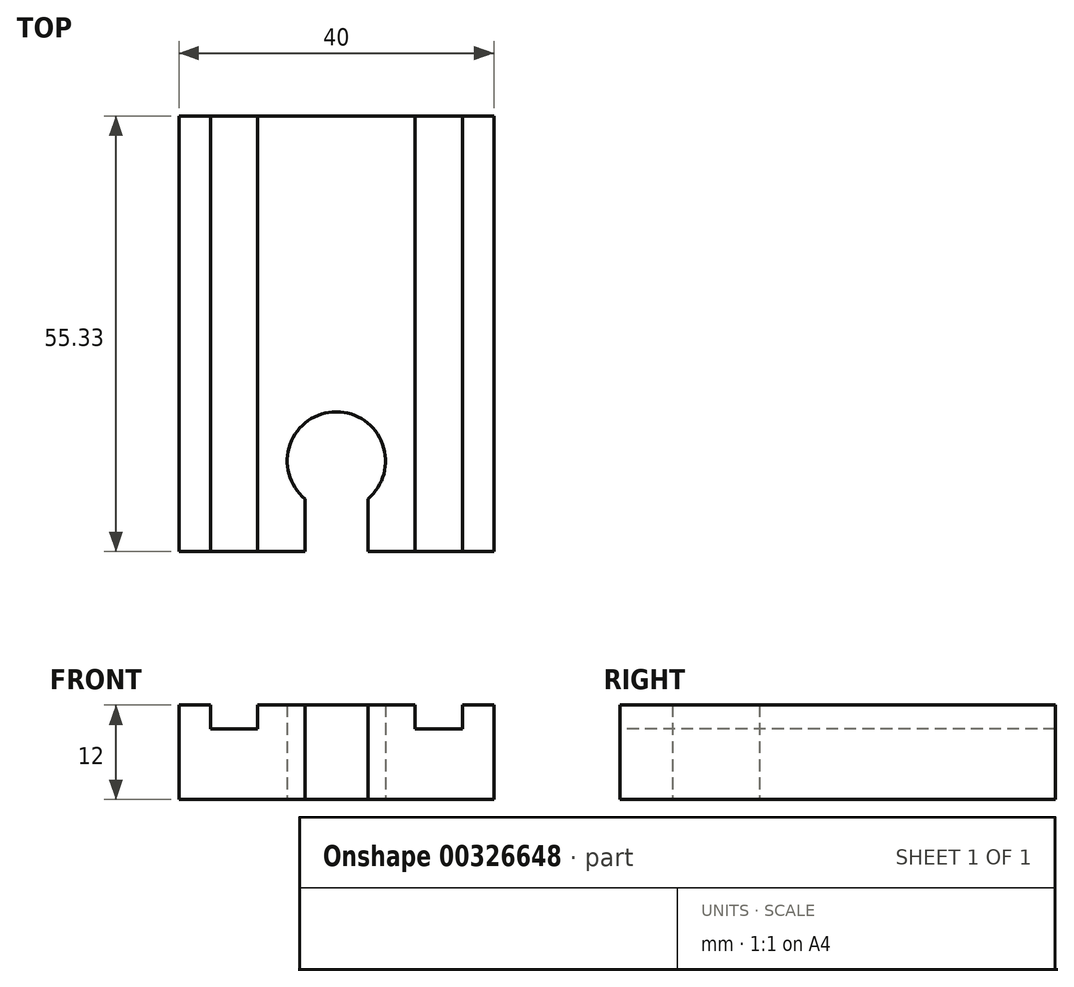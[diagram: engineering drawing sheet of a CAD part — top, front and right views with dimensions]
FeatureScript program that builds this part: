
annotation { "Feature Type Name" : "Feature", "Feature Type Description" : "" }
export const myFeature = defineFeature(function(context is Context, id is Id, definition is map)
    precondition{}
    {
        {
            var Q0;
            Q0=qCreatedBy(makeId("Top.planeOp"),FACE);
            var sketch = newSketch(context, id + "F0", { "sketchPlane" : qUnion([Q0])});
            skLineSegment(sketch, "E0.bottom", {"start": v(0, 0) * mm, "end": v(40, 0) * mm});
            skLineSegment(sketch, "E0.top", {"start": v(0, 55.33) * mm, "end": v(40, 55.33) * mm});
            skLineSegment(sketch, "E0.left", {"start": v(0, 0) * mm, "end": v(0, 55.33) * mm});
            skLineSegment(sketch, "E0.right", {"start": v(40, 0) * mm, "end": v(40, 55.33) * mm});
            skLineSegment(sketch, "E1", {"start": v(4, 0) * mm, "end": v(4, 55.33) * mm, "construction": true});
            skLineSegment(sketch, "E2", {"start": v(10, 55.33) * mm, "end": v(10, 0) * mm, "construction": true});
            skLineSegment(sketch, "E3", {"start": v(30, 55.33) * mm, "end": v(30, 0) * mm, "construction": true});
            skLineSegment(sketch, "E4", {"start": v(36, 55.33) * mm, "end": v(36, 0) * mm, "construction": true});
            skPoint(sketch, "E5", {"position": v(20, 0) * mm});
            skPoint(sketch, "E6", {"position": v(20, 55.33) * mm});
            skLineSegment(sketch, "E7.right", {"start": v(17.5, 55.33) * mm, "end": v(17.5, 62.15) * mm});
            skLineSegment(sketch, "E8", {"start": v(22.5, 62.15) * mm, "end": v(22.5, 55.33) * mm});
            skLineSegment(sketch, "E9", {"start": v(20, 67.33) * mm, "end": v(20, 55.33) * mm, "construction": true});
            skLineSegment(sketch, "E10", {"start": v(20, 0) * mm, "end": v(20, 11.5) * mm, "construction": true});
            skLineSegment(sketch, "E11", {"start": v(16, 0) * mm, "end": v(16, 6.7) * mm});
            skLineSegment(sketch, "E12", {"start": v(24, 0) * mm, "end": v(24, 6.7) * mm});
            skArc(sketch, "E13", {"start": v(16, 6.7) * mm, "mid": v(20, 5.25) * mm, "end": v(24, 6.7) * mm, "construction": true});
            skArc(sketch, "E14", {"start": v(24, 6.7) * mm, "mid": v(20, 17.75) * mm, "end": v(16, 6.7) * mm});
            skArc(sketch, "E15", {"start": v(17.5, 62.15) * mm, "mid": v(20, 61.58) * mm, "end": v(22.5, 62.15) * mm, "construction": true});
            skArc(sketch, "E16", {"start": v(22.5, 62.15) * mm, "mid": v(20, 73.08) * mm, "end": v(17.5, 62.15) * mm});
            skSolve(sketch);
        }
        {
            var Q0;
            Q0=makeQuery(id+"F0.imprint","IMPRINT",FACE,{"disambiguationData":[TD([[makeQuery(id+"F0.imprint","IMPRINT",EDGE,{"derivedFrom":sQuery(id+"F0.wireOp",EDGE,"E0.bottom")}),1.0]])]});
            extrude(context, id + "F1", {"entities" : qUnion([Q0]), "depth" : 12 * mm});
        }
        {
            var Q0;
            Q0=makeQuery(id+"F1.opExtrude","CAP_FACE",FACE,{"disambiguationData":[OSD([sQuery(id+"F0.wireOp",EDGE,"E0.bottom"),sQuery(id+"F0.wireOp",EDGE,"E0.top"),sQuery(id+"F0.wireOp",EDGE,"E0.left"),sQuery(id+"F0.wireOp",EDGE,"E0.right")])],"isStart":false});
            var sketch = newSketch(context, id + "F2", { "sketchPlane" : qUnion([Q0])});
            skLineSegment(sketch, "E17.0", {"start": v(4, 0) * mm, "end": v(4, 55.33) * mm});
            skLineSegment(sketch, "E17.1", {"start": v(10, 55.33) * mm, "end": v(10, 0) * mm});
            skLineSegment(sketch, "E17.2", {"start": v(30, 55.33) * mm, "end": v(30, 0) * mm});
            skLineSegment(sketch, "E17.3", {"start": v(36, 55.33) * mm, "end": v(36, 0) * mm});
            skLineSegment(sketch, "E18", {"start": v(4, 55.33) * mm, "end": v(10, 55.33) * mm});
            skLineSegment(sketch, "E19", {"start": v(4, 0) * mm, "end": v(10, 0) * mm});
            skLineSegment(sketch, "E20", {"start": v(30, 0) * mm, "end": v(36, 0) * mm});
            skLineSegment(sketch, "E21", {"start": v(30, 55.33) * mm, "end": v(36, 55.33) * mm});
            skSolve(sketch);
        }
        {
            var Q0;
            Q0=makeQuery(id+"F2.imprint","IMPRINT",FACE,{"disambiguationData":[TD([[makeQuery(id+"F2.imprint","IMPRINT",EDGE,{"derivedFrom":sQuery(id+"F2.wireOp",EDGE,"E17.0")}),-1.0]])]});
            var Q1;
            Q1=makeQuery(id+"F2.imprint","IMPRINT",FACE,{"disambiguationData":[TD([[makeQuery(id+"F2.imprint","IMPRINT",EDGE,{"derivedFrom":sQuery(id+"F2.wireOp",EDGE,"E17.2")}),1.0]])]});
            extrude(context, id + "F3", {"entities" : qUnion([Q0, Q1]), "operationType" : NewBodyOperationType.REMOVE, "oppositeDirection" : true, "depth" : 3 * mm});
        }
    });
